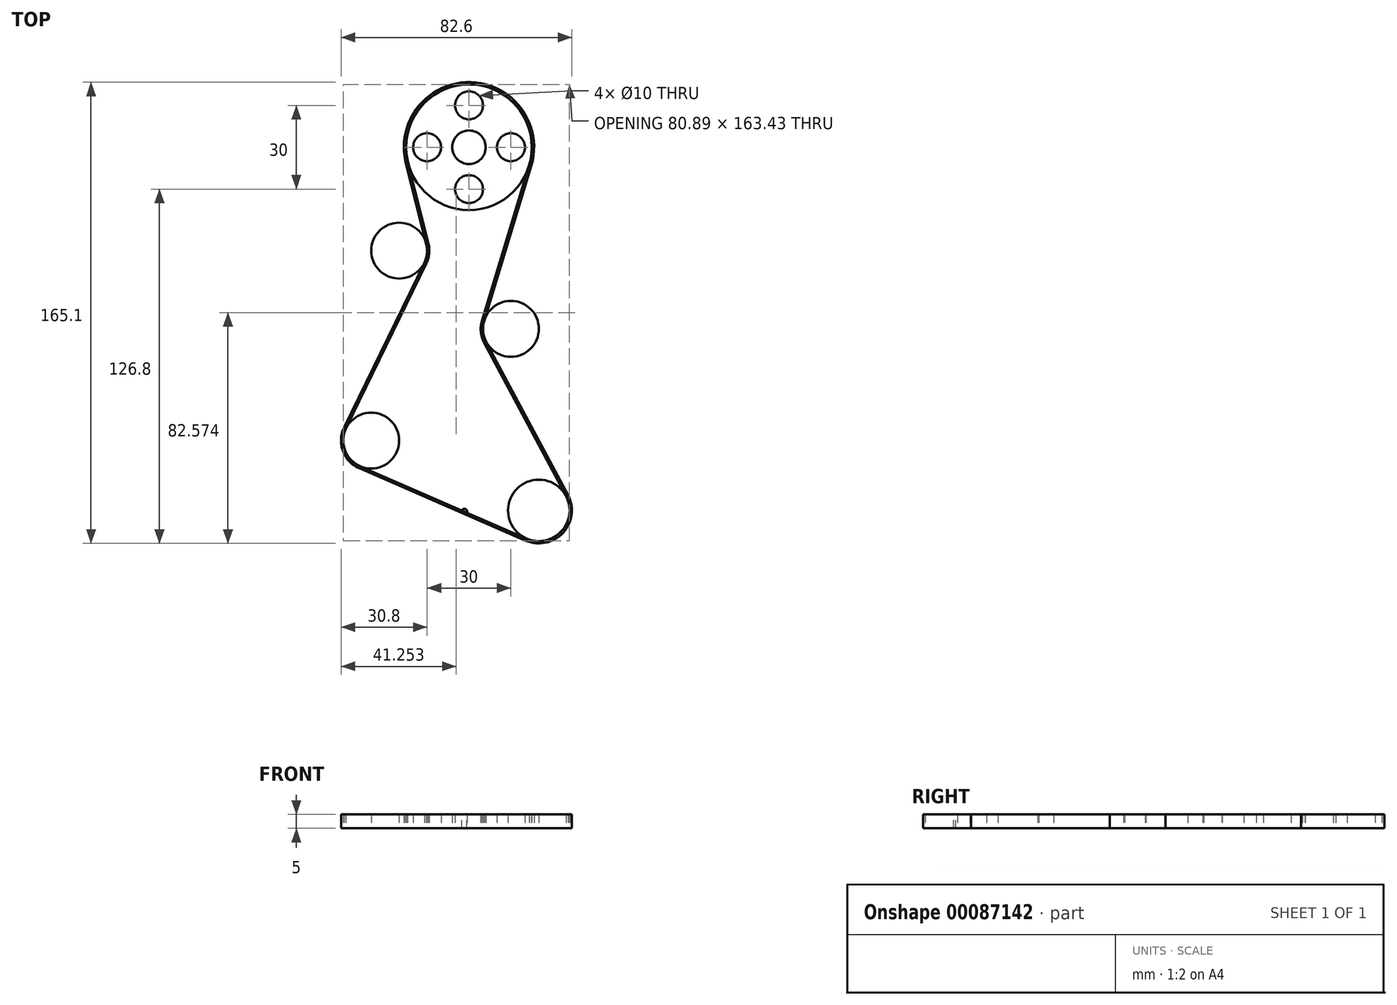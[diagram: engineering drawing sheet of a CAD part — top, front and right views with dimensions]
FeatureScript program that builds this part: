
annotation { "Feature Type Name" : "Feature", "Feature Type Description" : "" }
export const myFeature = defineFeature(function(context is Context, id is Id, definition is map)
    precondition{}
    {
        {
            var Q0;
            Q0=qCreatedBy(makeId("Top.planeOp"),FACE);
            var sketch = newSketch(context, id + "F0", { "sketchPlane" : qUnion([Q0])});
            skCircle(sketch, "E0", {"center": v(0, 80) * mm, "radius": 22.5 * mm});
            skCircle(sketch, "E1", {"center": v(-25, 43) * mm, "radius": 10 * mm});
            skCircle(sketch, "E2", {"center": v(15, 15) * mm, "radius": 10 * mm});
            skCircle(sketch, "E3", {"center": v(-35, -25) * mm, "radius": 10 * mm});
            skCircle(sketch, "E4", {"center": v(25, -50) * mm, "radius": 11 * mm});
            skCircle(sketch, "E5", {"center": v(0, 80) * mm, "radius": 6 * mm});
            skCircle(sketch, "E6", {"center": v(0, 95) * mm, "radius": 5 * mm});
            skCircle(sketch, "E7.1.0", {"center": v(-15, 80) * mm, "radius": 5 * mm});
            skCircle(sketch, "E7.2.0", {"center": v(0, 65) * mm, "radius": 5 * mm});
            skCircle(sketch, "E7.3.0", {"center": v(15, 80) * mm, "radius": 5 * mm});
            skSolve(sketch);
        }
        {
            var Q0;
            Q0=makeQuery(id+"F0.imprint","IMPRINT",FACE,{"disambiguationData":[TD([[makeQuery(id+"F0.imprint","IMPRINT",EDGE,{"derivedFrom":sQuery(id+"F0.wireOp",EDGE,"E1")}),1.0]])]});
            var Q1;
            Q1=makeQuery(id+"F0.imprint","IMPRINT",FACE,{"disambiguationData":[TD([[makeQuery(id+"F0.imprint","IMPRINT",EDGE,{"derivedFrom":sQuery(id+"F0.wireOp",EDGE,"E2")}),1.0]])]});
            var Q2;
            Q2=makeQuery(id+"F0.imprint","IMPRINT",FACE,{"disambiguationData":[TD([[makeQuery(id+"F0.imprint","IMPRINT",EDGE,{"derivedFrom":sQuery(id+"F0.wireOp",EDGE,"E3")}),1.0]])]});
            var Q3;
            Q3=makeQuery(id+"F0.imprint","IMPRINT",FACE,{"disambiguationData":[TD([[makeQuery(id+"F0.imprint","IMPRINT",EDGE,{"derivedFrom":sQuery(id+"F0.wireOp",EDGE,"E4")}),1.0]])]});
            var Q4;
            Q4=makeQuery(id+"F0.imprint","IMPRINT",FACE,{"disambiguationData":[TD([[makeQuery(id+"F0.imprint","IMPRINT",EDGE,{"derivedFrom":sQuery(id+"F0.wireOp",EDGE,"E0")}),1.0]])]});
            extrude(context, id + "F1", {"entities" : qUnion([Q0, Q1, Q2, Q3, Q4]), "depth" : 5 * mm});
        }
        {
            var Q0;
            Q0=qCreatedBy(makeId("Top.planeOp"),FACE);
            var sketch = newSketch(context, id + "F2", { "sketchPlane" : qUnion([Q0])});
            skArc(sketch, "E8.0", {"start": v(21.61, 73.74) * mm, "mid": v(0.69, 102.49) * mm, "end": v(-21.95, 75.07) * mm});
            skArc(sketch, "E8.1", {"start": v(-15.96, 38.73) * mm, "mid": v(-15.06, 41.9) * mm, "end": v(-15.24, 45.2) * mm});
            skArc(sketch, "E8.2", {"start": v(5.4, 17.78) * mm, "mid": v(5.05, 14.02) * mm, "end": v(6.12, 10.4) * mm});
            skArc(sketch, "E8.3", {"start": v(-44.04, -20.73) * mm, "mid": v(-44.36, -28.52) * mm, "end": v(-38.99, -34.17) * mm});
            skArc(sketch, "E8.4", {"start": v(20.61, -60.09) * mm, "mid": v(33.04, -57.51) * mm, "end": v(34.77, -44.94) * mm});
            skArc(sketch, "E9.0", {"start": v(22.38, 73.51) * mm, "mid": v(0.71, 103.29) * mm, "end": v(-22.73, 74.9) * mm});
            skArc(sketch, "E10.0", {"start": v(-15.23, 38.39) * mm, "mid": v(-14.27, 41.81) * mm, "end": v(-14.46, 45.37) * mm});
            skArc(sketch, "E11.0", {"start": v(-44.77, -20.39) * mm, "mid": v(-45.1, -28.8) * mm, "end": v(-39.3, -34.9) * mm});
            skArc(sketch, "E12.0", {"start": v(4.63, 18) * mm, "mid": v(4.25, 13.95) * mm, "end": v(5.4, 10.04) * mm});
            skArc(sketch, "E13.0", {"start": v(20.3, -60.82) * mm, "mid": v(33.62, -58.06) * mm, "end": v(35.48, -44.58) * mm});
            skLineSegment(sketch, "E14", {"start": v(-22.73, 74.9) * mm, "end": v(-15.24, 45.2) * mm});
            skLineSegment(sketch, "E15", {"start": v(-21.95, 75.07) * mm, "end": v(-14.46, 45.37) * mm});
            skLineSegment(sketch, "E16", {"start": v(-15.23, 38.39) * mm, "end": v(-44.04, -20.73) * mm});
            skLineSegment(sketch, "E17", {"start": v(-15.96, 38.73) * mm, "end": v(-44.77, -20.39) * mm});
            skLineSegment(sketch, "E18", {"start": v(-39.3, -34.9) * mm, "end": v(20.3, -60.82) * mm});
            skLineSegment(sketch, "E19", {"start": v(20.61, -60.09) * mm, "end": v(-38.99, -34.17) * mm});
            skLineSegment(sketch, "E20", {"start": v(35.48, -44.58) * mm, "end": v(6.12, 10.4) * mm});
            skLineSegment(sketch, "E21", {"start": v(5.4, 10.04) * mm, "end": v(34.77, -44.94) * mm});
            skLineSegment(sketch, "E22", {"start": v(5.4, 17.78) * mm, "end": v(22.38, 73.51) * mm});
            skLineSegment(sketch, "E23", {"start": v(4.63, 18) * mm, "end": v(21.61, 73.74) * mm});
            skSolve(sketch);
        }
        {
            var Q0;
            Q0 = qSketchRegion(id + "F2", true);
            extrude(context, id + "F3", {"entities" : qUnion([Q0]), "depth" : 5 * mm});
        }
        {
            var Q0;
            Q0=makeQuery(id+"F3.opExtrude","SWEPT_FACE",FACE,{"disambiguationData":[OSD([sQuery(id+"F2.wireOp",EDGE,"E19")])]});
            var sketch = newSketch(context, id + "F4", { "sketchPlane" : qUnion([Q0])});
            skLineSegment(sketch, "E24.bottom", {"start": v(-17.58, 0) * mm, "end": v(-19.58, 0) * mm});
            skLineSegment(sketch, "E24.top", {"start": v(-17.58, 5) * mm, "end": v(-19.58, 5) * mm});
            skLineSegment(sketch, "E24.left", {"start": v(-17.58, 0) * mm, "end": v(-17.58, 5) * mm});
            skLineSegment(sketch, "E24.right", {"start": v(-19.58, 0) * mm, "end": v(-19.58, 5) * mm});
            skSolve(sketch);
        }
        {
            var Q0;
            Q0 = qSketchRegion(id + "F4", true);
            extrude(context, id + "F5", {"entities" : qUnion([Q0]), "depth" : 1 * mm});
        }
        {
            var Q0;
            Q0=makeQuery(id+"F5.opExtrude","CAP_EDGE",EDGE,{"disambiguationData":[OSD([sQuery(id+"F4.wireOp",EDGE,"E24.left")])],"isStart":false});
            var Q1;
            Q1=makeQuery(id+"F5.opExtrude","CAP_EDGE",EDGE,{"disambiguationData":[OSD([sQuery(id+"F4.wireOp",EDGE,"E24.right")])],"isStart":false});
            fillet(context, id + "F6", {"entities" : qUnion([Q0, Q1]), "radius" : 1 * mm, "tangentPropagation" : true, "allowEdgeOverflow" : false});
        }
    });
